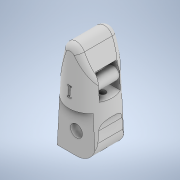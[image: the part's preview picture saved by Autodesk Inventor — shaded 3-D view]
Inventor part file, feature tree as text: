
AUTODESK INVENTOR PART (.ipt)
format: ipt  version: 2021 (Build 250183000, 183)  size: 356,864 bytes
history: native  units: mm
features: other x11, sketch x10, extrude x8, plane x5, fillet x4, hole x1
ambient origin geometry x8: Origin, YZ Plane, XZ Plane, XY Plane, X Axis, Y Axis, Z Axis, Center Point
bodies: Volumenkörper1 (feature_tree), Volumenkörper2 (feature_tree), Volumenkörper3 (feature_tree), Volumenkörper4 (feature_tree), Volumenkörper5 (feature_tree), Volumenkörper7 (feature_tree), Volumenkörper8 (feature_tree), Volumenkörper9 (feature_tree)
feature tree (39):
  extrude  "Extrusion1"  Depth=38.0mm TaperAngle=0.0deg
  other  "Flächenverjüngung1"
  extrude  "Extrusion2"  Depth=15.0mm
  fillet  "Rundung1"  Radius=30.0mm
  other  "Kombinieren1"
  fillet  "Rundung2"  Radius=5.0mm
  extrude  "Extrusion3"  Depth=4.8mm
  other  "Kombinieren2"
  hole  "Bohrung1"  [1 undecoded]
  extrude  "Extrusion4"  Depth=50.0mm TaperAngle=0.0deg
  other  "Kombinieren3"
  plane  "Arbeitsebene3"
  other  "Trennen2"
  fillet  "Rundung3"  [1 undecoded]
  plane  "Arbeitsebene4"
  extrude  "Extrusion6"  Depth=40.0mm
  plane  "Arbeitsebene5"
  extrude  "Extrusion8"  Depth=5.0mm
  extrude  "Extrusion9"  Depth=3.0mm
  other  "Kombinieren6"
  other  "Kombinieren7"
  extrude  "Extrusion10"  Depth=7.5mm
  other  "Kombinieren8"
  fillet  "Rundung4"  [1 undecoded]
  other  "Kombinieren9"
  plane  "Arbeitsebene7"
  other  "Prägen2"
  sketch  "Skizze1"  dims[d0=16.0mm d1=38.0mm d2=0.0mm]
  sketch  "Skizze2"  dims[d3=6.5mm d4=15.0mm d5=30.0mm d6=0.0mm d7=5.0mm]
  sketch  "Skizze3"  dims[d8=6.5mm d9=4.8mm]
  sketch  "Skizze4"  dims[d11=15.0mm d12=15.0mm]
  sketch  "Skizze5"  dims[d13=4.8mm d15=50.0mm d16=0.0mm]
  other  "Arbeitsachse1"
  plane  "Arbeitsebene2"
  sketch  "Skizze8"  dims[d17=4.0mm d18=6.0mm d19=4.0mm d20=2.0mm d21=90.0deg d22=8.0mm d23=20.594885mm d24=0.0mm]
  sketch  "Skizze10"  dims[d25=7.25mm d26=40.0mm]
  sketch  "Skizze11"  dims[d28=4.363323mm d29=5.0mm]
  sketch  "Skizze12"  dims[d30=30.0mm d31=0.0mm d32=3.0mm]
  sketch  "Skizze15"  dims[d33=-2.617994mm d34=5.0mm d35=3.0mm d36=-0.436332mm d43=-3.5mm d44=2.4mm d45=20.0mm d46=0.0mm d47=6.0mm d52=-1.0mm d53=7.0mm d54=8.0mm d55=18.0mm d56=3.5mm d57=20.0mm d58=0.0mm d59=2.0mm d60=4.0mm d61=0.0mm d62=23.25mm d63=0.0mm d64=4.0mm d65=4.0mm d66=7.0mm d67=0.0mm d68=2.0mm d69=22.0mm d76=7.5mm d78=0.9mm d79=17.5mm d80=4.0mm d81=0.5mm d82=0.0mm]
note: 3 required parameter values undecoded (feature->parameter linkage not recoverable at this tier; creation-order binding heuristic only, values carry confidence <= 0.55)
